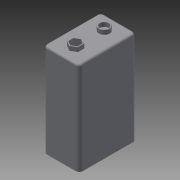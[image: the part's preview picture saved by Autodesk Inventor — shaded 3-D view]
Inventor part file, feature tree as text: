
AUTODESK INVENTOR PART (.ipt)
format: ipt  version: 2015 (Build 190159000, 159)  size: 187,392 bytes
history: native  units: in
note: dims shown in document units (in); Inventor stores cm internally (conversion verified against a paired STEP export)
features: fillet x5, extrude x3, sketch x3, shell x2
ambient origin geometry x8: Origin, YZ Plane, XZ Plane, XY Plane, X Axis, Y Axis, Z Axis, Center Point
bodies: Solid1 (feature_tree)
feature tree (13):
  extrude  "Extrusion1"  Depth=0.8in
  extrude  "Extrusion2"  Depth=1.3in TaperAngle=0.0deg
  shell  "Shell1"  Thickness=0.5in
  extrude  "Extrusion3"  Depth=0.5in
  shell  "Shell2"  Thickness=0.06in
  fillet  "Fillet1"  Radius=0.015in
  fillet  "Fillet2"  Radius=0.15in
  fillet  "Fillet3"  Radius=0.25in
  fillet  "Fillet4"  Radius=0.2in
  fillet  "Fillet5"  Radius=0.06in
  sketch  "Sketch1"  dims[d0=0.5in d1=0.8in]
  sketch  "Sketch2"  dims[d2=0.05in d3=1.3in d4=0.0in d6=0.5in]
  sketch  "Sketch3"  dims[d7=0.25in d8=0.2in d9=0.06in d10=0.0in d11=0.015in d12=0.15in d13=0.25in d14=0.2in d15=0.06in d16=0.0in d17=0.015in d18=0.01in d19=0.005in d20=0.005in d21=0.005in d22=0.03in d23=0.5in d24=0.18in]
